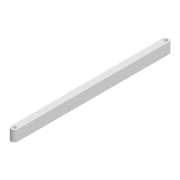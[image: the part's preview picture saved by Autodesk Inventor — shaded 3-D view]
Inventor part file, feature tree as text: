
AUTODESK INVENTOR PART (.ipt)
format: ipt  version: 2022 (Build 260153000, 153)  size: 88,064 bytes
history: native  units: mm
features: extrude x1, sketch x1
ambient origin geometry x8: Origin, YZ Plane, XZ Plane, XY Plane, X Axis, Y Axis, Z Axis, Center Point
bodies: Solid1 (feature_tree)
feature tree (2):
  extrude  "Extrusion1"  Depth=141.096mm
  sketch  "Sketch1"  dims[d0=6.0mm d1=141.096mm d2=3.0mm d3=3.0mm d4=10.0mm d5=0.0mm]
